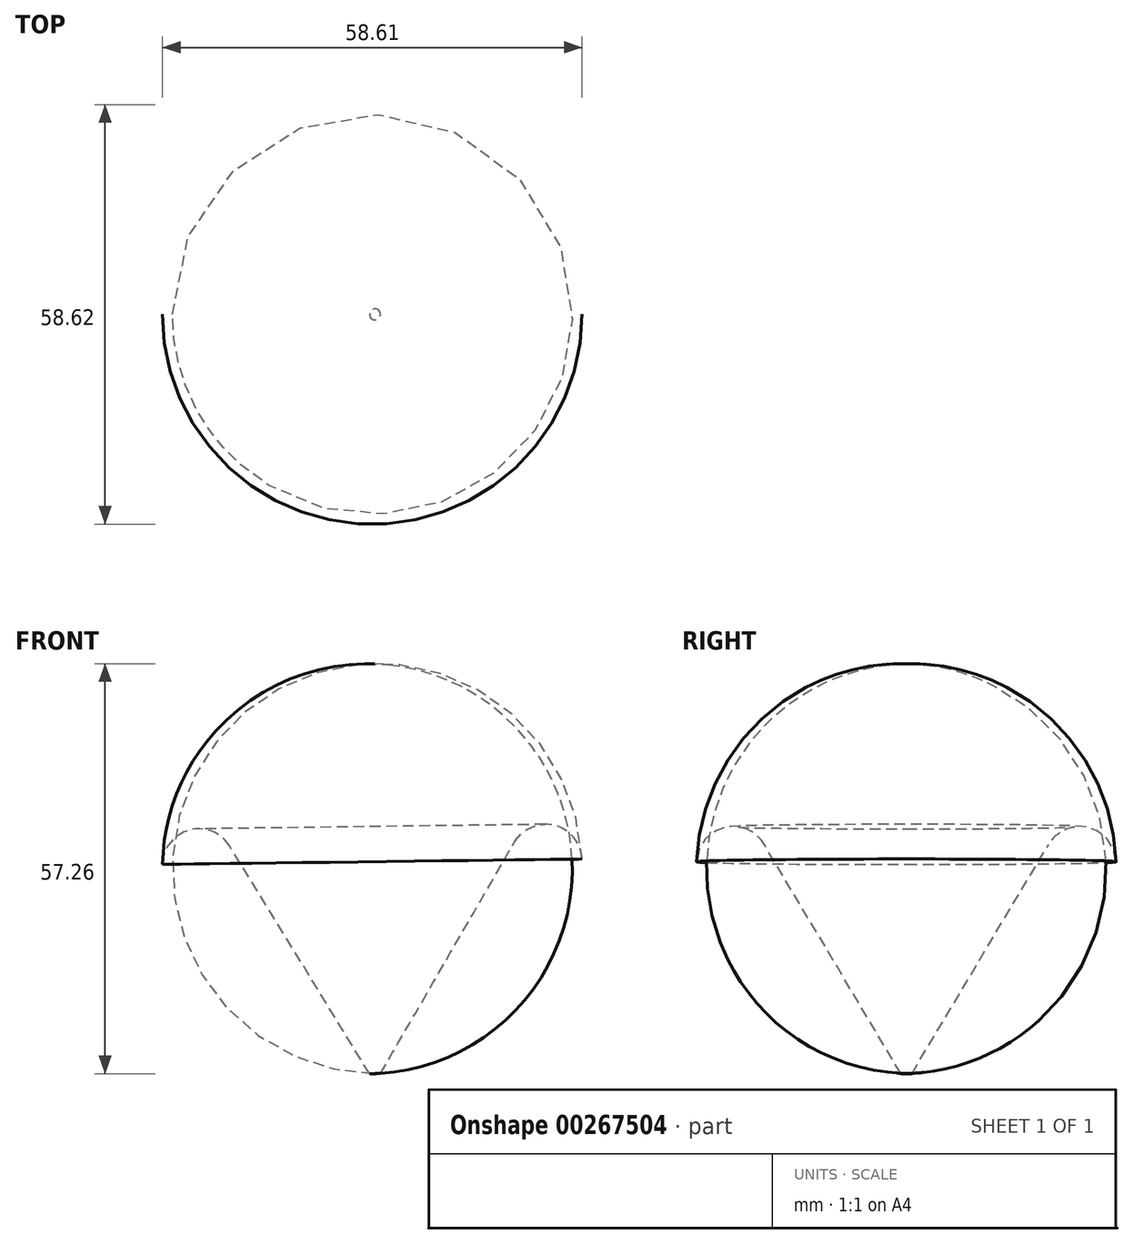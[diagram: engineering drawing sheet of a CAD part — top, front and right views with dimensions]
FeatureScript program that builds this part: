
annotation { "Feature Type Name" : "Feature", "Feature Type Description" : "" }
export const myFeature = defineFeature(function(context is Context, id is Id, definition is map)
    precondition{}
    {
        {
            var Q0;
            Q0=qCreatedBy(makeId("Front.planeOp"),FACE);
            var sketch = newSketch(context, id + "F0", { "sketchPlane" : qUnion([Q0])});
            skLineSegment(sketch, "E0", {"start": v(31.14, 28.58) * mm, "end": v(0, -25.22) * mm});
            skArc(sketch, "E1", {"start": v(0, -25.22) * mm, "mid": v(24.33, -10.94) * mm, "end": v(24.6, 17.27) * mm});
            skLineSegment(sketch, "E2", {"start": v(24.6, 17.27) * mm, "end": v(0, -25.22) * mm});
            skLineSegment(sketch, "E3", {"start": v(-1.77, 52.03) * mm, "end": v(-0.44, -50.45) * mm});
            skSolve(sketch);
        }
        {
            var Q0;
            Q0=makeQuery(id+"F0.imprint","IMPRINT",FACE,{"disambiguationData":[TD([[makeQuery(id+"F0.imprint","IMPRINT",EDGE,{"derivedFrom":sQuery(id+"F0.wireOp",EDGE,"E1")}),1.0]])]});
            var Q1;
            Q1=sQuery(id+"F0.wireOp",EDGE,"E3");
            revolve(context, id + "F1", {"entities" : qUnion([Q0]), "axis" : qUnion([Q1]), "revolveType" : RevolveType.FULL});
        }
        {
            var Q0;
            {var subQ0=sQuery(id+"F0.wireOp",EDGE,"E2");var subQ1=sQuery(id+"F0.wireOp",EDGE,"E1");Q0=makeQuery(id+"F1.opRevolve","SWEPT_EDGE",EDGE,{"disambiguationData":[OSD([subQ1,subQ0]),TDD([makeQuery(id+"F0.imprint","INTERSECT",VERTEX,{"disambiguationData":[OD(0.0)],"derivedFrom":[subQ1,subQ0]})])]});}
            fillet(context, id + "F2", {"entities" : qUnion([Q0]), "radius" : 5.08 * mm, "tangentPropagation" : true, "allowEdgeOverflow" : false});
        }
    });
